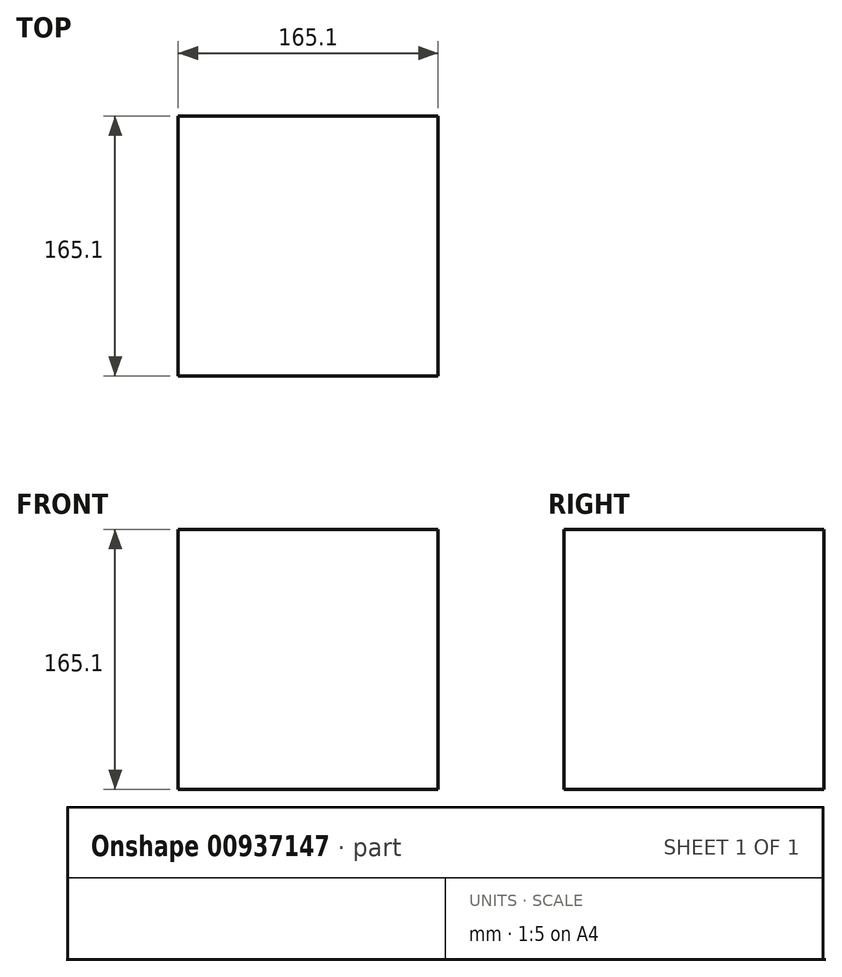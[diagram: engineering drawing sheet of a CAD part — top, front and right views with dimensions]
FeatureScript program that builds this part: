
annotation { "Feature Type Name" : "Feature", "Feature Type Description" : "" }
export const myFeature = defineFeature(function(context is Context, id is Id, definition is map)
    precondition{}
    {
        {
            assignVariable(context, id + "F0", {"name" : "size", "anyValue" : 165.1 * mm});
        }
        {
            var Q0;
            Q0=qCreatedBy(makeId("Front.planeOp"),FACE);
            var sketch = newSketch(context, id + "F1", { "sketchPlane" : qUnion([Q0])});
            skLineSegment(sketch, "E0.bottom", {"start": v(41.45, -147.43) * mm, "end": v(-123.65, -147.43) * mm});
            skLineSegment(sketch, "E0.top", {"start": v(41.45, 17.67) * mm, "end": v(-123.65, 17.67) * mm});
            skLineSegment(sketch, "E0.left", {"start": v(41.45, -147.43) * mm, "end": v(41.45, 17.67) * mm});
            skLineSegment(sketch, "E0.right", {"start": v(-123.65, -147.43) * mm, "end": v(-123.65, 17.67) * mm});
            skSolve(sketch);
        }
        {
            var Q0;
            Q0 = qSketchRegion(id + "F1", true);
            extrude(context, id + "F2", {"entities" : qUnion([Q0]), "depth" : getVariable(context, 'size'), "offsetDistance" : 25.4 * mm});
        }
    });
